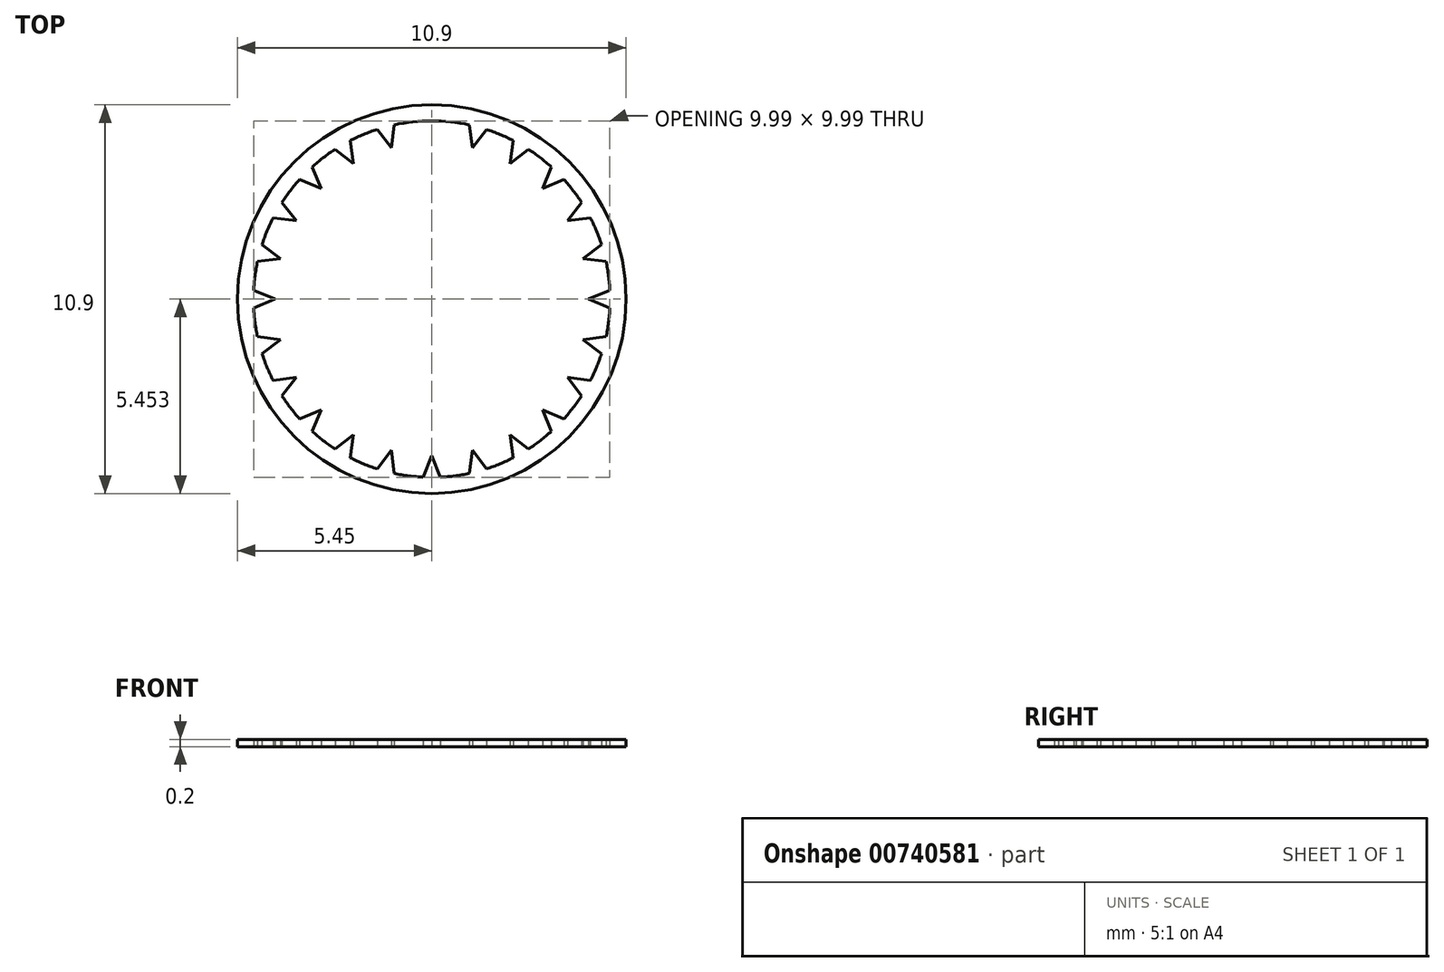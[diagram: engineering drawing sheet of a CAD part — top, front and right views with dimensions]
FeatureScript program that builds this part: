
annotation { "Feature Type Name" : "Feature", "Feature Type Description" : "" }
export const myFeature = defineFeature(function(context is Context, id is Id, definition is map)
    precondition{}
    {
        {
            var Q0;
            Q0=qCreatedBy(makeId("Top.planeOp"),FACE);
            var sketch = newSketch(context, id + "F0", { "sketchPlane" : qUnion([Q0])});
            skCircle(sketch, "E0", {"center": v(0, 0) * mm, "radius": 5.45 * mm});
            skCircle(sketch, "E1", {"center": v(0, 0) * mm, "radius": 5 * mm});
            skLineSegment(sketch, "E2", {"start": v(0, 4.4) * mm, "end": v(-0.25, 5) * mm});
            skLineSegment(sketch, "E3.MirrorCS", {"start": v(0, 4.4) * mm, "end": v(0.25, 5) * mm});
            skLineSegment(sketch, "E4.anchor1", {"start": v(0, 0) * mm, "end": v(0, 4.4) * mm, "construction": true});
            skLineSegment(sketch, "E4.anchor2", {"start": v(0, 0) * mm, "end": v(0, 4.4) * mm, "construction": true});
            skLineSegment(sketch, "E5.1.0", {"start": v(-1.14, 4.24) * mm, "end": v(-1.53, 4.76) * mm});
            skLineSegment(sketch, "E5.1.1", {"start": v(-1.14, 4.24) * mm, "end": v(-1.06, 4.89) * mm});
            skLineSegment(sketch, "E5.2.0", {"start": v(-2.2, 3.8) * mm, "end": v(-2.7, 4.2) * mm});
            skLineSegment(sketch, "E5.2.1", {"start": v(-2.2, 3.8) * mm, "end": v(-2.28, 4.45) * mm});
            skLineSegment(sketch, "E5.3.0", {"start": v(-3.1, 3.1) * mm, "end": v(-3.7, 3.36) * mm});
            skLineSegment(sketch, "E5.3.1", {"start": v(-3.1, 3.1) * mm, "end": v(-3.36, 3.7) * mm});
            skLineSegment(sketch, "E5.4.0", {"start": v(-3.8, 2.2) * mm, "end": v(-4.45, 2.28) * mm});
            skLineSegment(sketch, "E5.4.1", {"start": v(-3.8, 2.2) * mm, "end": v(-4.2, 2.7) * mm});
            skLineSegment(sketch, "E5.5.0", {"start": v(-4.24, 1.14) * mm, "end": v(-4.89, 1.06) * mm});
            skLineSegment(sketch, "E5.5.1", {"start": v(-4.24, 1.14) * mm, "end": v(-4.76, 1.53) * mm});
            skLineSegment(sketch, "E5.6.0", {"start": v(-4.4, 0) * mm, "end": v(-5, -0.25) * mm});
            skLineSegment(sketch, "E5.6.1", {"start": v(-4.4, 0) * mm, "end": v(-5, 0.25) * mm});
            skLineSegment(sketch, "E5.7.0", {"start": v(-4.24, -1.14) * mm, "end": v(-4.76, -1.53) * mm});
            skLineSegment(sketch, "E5.7.1", {"start": v(-4.24, -1.14) * mm, "end": v(-4.89, -1.06) * mm});
            skLineSegment(sketch, "E5.8.0", {"start": v(-3.8, -2.2) * mm, "end": v(-4.2, -2.7) * mm});
            skLineSegment(sketch, "E5.8.1", {"start": v(-3.8, -2.2) * mm, "end": v(-4.45, -2.28) * mm});
            skLineSegment(sketch, "E5.9.0", {"start": v(-3.1, -3.1) * mm, "end": v(-3.36, -3.7) * mm});
            skLineSegment(sketch, "E5.9.1", {"start": v(-3.1, -3.1) * mm, "end": v(-3.7, -3.36) * mm});
            skLineSegment(sketch, "E5.10.0", {"start": v(-2.2, -3.8) * mm, "end": v(-2.28, -4.45) * mm});
            skLineSegment(sketch, "E5.10.1", {"start": v(-2.2, -3.8) * mm, "end": v(-2.7, -4.2) * mm});
            skLineSegment(sketch, "E5.11.0", {"start": v(-1.14, -4.24) * mm, "end": v(-1.06, -4.89) * mm});
            skLineSegment(sketch, "E5.11.1", {"start": v(-1.14, -4.24) * mm, "end": v(-1.53, -4.76) * mm});
            skLineSegment(sketch, "E5.12.0", {"start": v(0, -4.4) * mm, "end": v(0.25, -5) * mm});
            skLineSegment(sketch, "E5.12.1", {"start": v(0, -4.4) * mm, "end": v(-0.25, -5) * mm});
            skLineSegment(sketch, "E5.13.0", {"start": v(1.14, -4.24) * mm, "end": v(1.53, -4.76) * mm});
            skLineSegment(sketch, "E5.13.1", {"start": v(1.14, -4.24) * mm, "end": v(1.06, -4.89) * mm});
            skLineSegment(sketch, "E5.14.0", {"start": v(2.2, -3.8) * mm, "end": v(2.7, -4.2) * mm});
            skLineSegment(sketch, "E5.14.1", {"start": v(2.2, -3.8) * mm, "end": v(2.28, -4.45) * mm});
            skLineSegment(sketch, "E5.15.0", {"start": v(3.1, -3.1) * mm, "end": v(3.7, -3.36) * mm});
            skLineSegment(sketch, "E5.15.1", {"start": v(3.1, -3.1) * mm, "end": v(3.36, -3.7) * mm});
            skLineSegment(sketch, "E5.16.0", {"start": v(3.8, -2.2) * mm, "end": v(4.45, -2.28) * mm});
            skLineSegment(sketch, "E5.16.1", {"start": v(3.8, -2.2) * mm, "end": v(4.2, -2.7) * mm});
            skLineSegment(sketch, "E5.17.0", {"start": v(4.24, -1.14) * mm, "end": v(4.89, -1.06) * mm});
            skLineSegment(sketch, "E5.17.1", {"start": v(4.24, -1.14) * mm, "end": v(4.76, -1.53) * mm});
            skLineSegment(sketch, "E5.18.0", {"start": v(4.4, 0) * mm, "end": v(5, 0.25) * mm});
            skLineSegment(sketch, "E5.18.1", {"start": v(4.4, 0) * mm, "end": v(5, -0.25) * mm});
            skLineSegment(sketch, "E5.19.0", {"start": v(4.24, 1.14) * mm, "end": v(4.76, 1.53) * mm});
            skLineSegment(sketch, "E5.19.1", {"start": v(4.24, 1.14) * mm, "end": v(4.89, 1.06) * mm});
            skLineSegment(sketch, "E5.20.0", {"start": v(3.8, 2.2) * mm, "end": v(4.2, 2.7) * mm});
            skLineSegment(sketch, "E5.20.1", {"start": v(3.8, 2.2) * mm, "end": v(4.45, 2.28) * mm});
            skLineSegment(sketch, "E5.21.0", {"start": v(3.1, 3.1) * mm, "end": v(3.36, 3.7) * mm});
            skLineSegment(sketch, "E5.21.1", {"start": v(3.1, 3.1) * mm, "end": v(3.7, 3.36) * mm});
            skLineSegment(sketch, "E5.22.0", {"start": v(2.2, 3.8) * mm, "end": v(2.28, 4.45) * mm});
            skLineSegment(sketch, "E5.22.1", {"start": v(2.2, 3.8) * mm, "end": v(2.7, 4.2) * mm});
            skLineSegment(sketch, "E5.23.0", {"start": v(1.14, 4.24) * mm, "end": v(1.06, 4.89) * mm});
            skLineSegment(sketch, "E5.23.1", {"start": v(1.14, 4.24) * mm, "end": v(1.53, 4.76) * mm});
            skSolve(sketch);
        }
        {
            var Q0;
            Q0=makeQuery(id+"F0.imprint","IMPRINT",FACE,{"disambiguationData":[TD([[makeQuery(id+"F0.imprint","IMPRINT",EDGE,{"derivedFrom":sQuery(id+"F0.wireOp",EDGE,"E0")}),1.0]])]});
            var Q1;
            {var subQ0=sQuery(id+"F0.wireOp",EDGE,"E5.2.0");Q1=makeQuery(id+"F0.imprint","IMPRINT",FACE,{"disambiguationData":[TD([[makeQuery(id+"F0.imprint","IMPRINT",EDGE,{"derivedFrom":subQ0}),-1.0]])]});}
            var Q2;
            {var subQ0=sQuery(id+"F0.wireOp",EDGE,"E5.1.0");Q2=makeQuery(id+"F0.imprint","IMPRINT",FACE,{"disambiguationData":[TD([[makeQuery(id+"F0.imprint","IMPRINT",EDGE,{"derivedFrom":subQ0}),-1.0]])]});}
            var Q3;
            {var subQ0=sQuery(id+"F0.wireOp",EDGE,"E5.3.0");Q3=makeQuery(id+"F0.imprint","IMPRINT",FACE,{"disambiguationData":[TD([[makeQuery(id+"F0.imprint","IMPRINT",EDGE,{"derivedFrom":subQ0}),-1.0]])]});}
            var Q4;
            {var subQ0=sQuery(id+"F0.wireOp",EDGE,"E5.4.0");Q4=makeQuery(id+"F0.imprint","IMPRINT",FACE,{"disambiguationData":[TD([[makeQuery(id+"F0.imprint","IMPRINT",EDGE,{"derivedFrom":subQ0}),-1.0]])]});}
            var Q5;
            {var subQ0=sQuery(id+"F0.wireOp",EDGE,"E5.5.0");Q5=makeQuery(id+"F0.imprint","IMPRINT",FACE,{"disambiguationData":[TD([[makeQuery(id+"F0.imprint","IMPRINT",EDGE,{"derivedFrom":subQ0}),-1.0]])]});}
            var Q6;
            {var subQ0=sQuery(id+"F0.wireOp",EDGE,"E5.6.0");Q6=makeQuery(id+"F0.imprint","IMPRINT",FACE,{"disambiguationData":[TD([[makeQuery(id+"F0.imprint","IMPRINT",EDGE,{"derivedFrom":subQ0}),-1.0]])]});}
            var Q7;
            {var subQ0=sQuery(id+"F0.wireOp",EDGE,"E5.7.0");Q7=makeQuery(id+"F0.imprint","IMPRINT",FACE,{"disambiguationData":[TD([[makeQuery(id+"F0.imprint","IMPRINT",EDGE,{"derivedFrom":subQ0}),-1.0]])]});}
            var Q8;
            {var subQ0=sQuery(id+"F0.wireOp",EDGE,"E5.8.0");Q8=makeQuery(id+"F0.imprint","IMPRINT",FACE,{"disambiguationData":[TD([[makeQuery(id+"F0.imprint","IMPRINT",EDGE,{"derivedFrom":subQ0}),-1.0]])]});}
            var Q9;
            {var subQ0=sQuery(id+"F0.wireOp",EDGE,"E5.9.0");Q9=makeQuery(id+"F0.imprint","IMPRINT",FACE,{"disambiguationData":[TD([[makeQuery(id+"F0.imprint","IMPRINT",EDGE,{"derivedFrom":subQ0}),-1.0]])]});}
            var Q10;
            {var subQ0=sQuery(id+"F0.wireOp",EDGE,"E5.10.0");Q10=makeQuery(id+"F0.imprint","IMPRINT",FACE,{"disambiguationData":[TD([[makeQuery(id+"F0.imprint","IMPRINT",EDGE,{"derivedFrom":subQ0}),-1.0]])]});}
            var Q11;
            {var subQ0=sQuery(id+"F0.wireOp",EDGE,"E5.11.0");Q11=makeQuery(id+"F0.imprint","IMPRINT",FACE,{"disambiguationData":[TD([[makeQuery(id+"F0.imprint","IMPRINT",EDGE,{"derivedFrom":subQ0}),-1.0]])]});}
            var Q12;
            {var subQ0=sQuery(id+"F0.wireOp",EDGE,"E5.12.0");Q12=makeQuery(id+"F0.imprint","IMPRINT",FACE,{"disambiguationData":[TD([[makeQuery(id+"F0.imprint","IMPRINT",EDGE,{"derivedFrom":subQ0}),-1.0]])]});}
            var Q13;
            {var subQ0=sQuery(id+"F0.wireOp",EDGE,"E5.13.0");Q13=makeQuery(id+"F0.imprint","IMPRINT",FACE,{"disambiguationData":[TD([[makeQuery(id+"F0.imprint","IMPRINT",EDGE,{"derivedFrom":subQ0}),-1.0]])]});}
            var Q14;
            {var subQ0=sQuery(id+"F0.wireOp",EDGE,"E5.14.0");Q14=makeQuery(id+"F0.imprint","IMPRINT",FACE,{"disambiguationData":[TD([[makeQuery(id+"F0.imprint","IMPRINT",EDGE,{"derivedFrom":subQ0}),-1.0]])]});}
            var Q15;
            {var subQ0=sQuery(id+"F0.wireOp",EDGE,"E5.15.0");Q15=makeQuery(id+"F0.imprint","IMPRINT",FACE,{"disambiguationData":[TD([[makeQuery(id+"F0.imprint","IMPRINT",EDGE,{"derivedFrom":subQ0}),-1.0]])]});}
            var Q16;
            {var subQ0=sQuery(id+"F0.wireOp",EDGE,"E5.16.0");Q16=makeQuery(id+"F0.imprint","IMPRINT",FACE,{"disambiguationData":[TD([[makeQuery(id+"F0.imprint","IMPRINT",EDGE,{"derivedFrom":subQ0}),-1.0]])]});}
            var Q17;
            {var subQ0=sQuery(id+"F0.wireOp",EDGE,"E5.17.0");Q17=makeQuery(id+"F0.imprint","IMPRINT",FACE,{"disambiguationData":[TD([[makeQuery(id+"F0.imprint","IMPRINT",EDGE,{"derivedFrom":subQ0}),-1.0]])]});}
            var Q18;
            {var subQ0=sQuery(id+"F0.wireOp",EDGE,"E5.18.0");Q18=makeQuery(id+"F0.imprint","IMPRINT",FACE,{"disambiguationData":[TD([[makeQuery(id+"F0.imprint","IMPRINT",EDGE,{"derivedFrom":subQ0}),-1.0]])]});}
            var Q19;
            {var subQ0=sQuery(id+"F0.wireOp",EDGE,"E5.19.0");Q19=makeQuery(id+"F0.imprint","IMPRINT",FACE,{"disambiguationData":[TD([[makeQuery(id+"F0.imprint","IMPRINT",EDGE,{"derivedFrom":subQ0}),-1.0]])]});}
            var Q20;
            {var subQ0=sQuery(id+"F0.wireOp",EDGE,"E5.20.0");Q20=makeQuery(id+"F0.imprint","IMPRINT",FACE,{"disambiguationData":[TD([[makeQuery(id+"F0.imprint","IMPRINT",EDGE,{"derivedFrom":subQ0}),-1.0]])]});}
            var Q21;
            {var subQ0=sQuery(id+"F0.wireOp",EDGE,"E5.21.0");Q21=makeQuery(id+"F0.imprint","IMPRINT",FACE,{"disambiguationData":[TD([[makeQuery(id+"F0.imprint","IMPRINT",EDGE,{"derivedFrom":subQ0}),-1.0]])]});}
            var Q22;
            {var subQ0=sQuery(id+"F0.wireOp",EDGE,"E5.22.0");Q22=makeQuery(id+"F0.imprint","IMPRINT",FACE,{"disambiguationData":[TD([[makeQuery(id+"F0.imprint","IMPRINT",EDGE,{"derivedFrom":subQ0}),-1.0]])]});}
            var Q23;
            {var subQ0=sQuery(id+"F0.wireOp",EDGE,"E5.23.0");Q23=makeQuery(id+"F0.imprint","IMPRINT",FACE,{"disambiguationData":[TD([[makeQuery(id+"F0.imprint","IMPRINT",EDGE,{"derivedFrom":subQ0}),-1.0]])]});}
            var Q24;
            {var subQ0=sQuery(id+"F0.wireOp",EDGE,"E2");Q24=makeQuery(id+"F0.imprint","IMPRINT",FACE,{"disambiguationData":[TD([[makeQuery(id+"F0.imprint","IMPRINT",EDGE,{"derivedFrom":subQ0}),-1.0]])]});}
            extrude(context, id + "F1", {"entities" : qUnion([Q0, Q1, Q2, Q3, Q4, Q5, Q6, Q7, Q8, Q9, Q10, Q11, Q12, Q13, Q14, Q15, Q16, Q17, Q18, Q19, Q20, Q21, Q22, Q23, Q24]), "depth" : 0.2 * mm, "offsetDistance" : 25 * mm});
        }
    });
